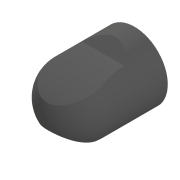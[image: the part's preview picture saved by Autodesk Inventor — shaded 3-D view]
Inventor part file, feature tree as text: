
AUTODESK INVENTOR PART (.ipt)
format: ipt  version: 2020 (Build 240168000, 168)  size: 396,800 bytes
history: native  units: mm
features: sketch x4, extrude x2, revolve x2, other x1
ambient origin geometry x8: Origin, YZ Plane, XZ Plane, XY Plane, X Axis, Y Axis, Z Axis, Center Point
bodies: Solid1 (feature_tree)
feature tree (9):
  extrude  "Extrusion1"  Depth=11.315mm TaperAngle=0.0deg
  revolve  "Revolution1"  [1 undecoded]
  extrude  "Extrusion2"  Depth=4.875mm
  revolve  "Revolution2"  [1 undecoded]
  sketch  "Sketch1"  dims[d0=13.5mm d1=11.315mm d2=0.0mm]
  sketch  "Sketch2"  dims[d3=90.0deg d55=15.315mm d56=0.0mm]
  sketch  "Sketch3"  dims[d57=4.875mm d58=1.45mm]
  other  "Image1"
  sketch  "Sketch4"  dims[d59=0.685mm d60=1.5mm d61=1.2847mm d63=14.3mm d64=3.1075mm d65=90.0deg]
note: 2 required parameter values undecoded (feature->parameter linkage not recoverable at this tier; creation-order binding heuristic only, values carry confidence <= 0.55)
